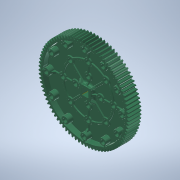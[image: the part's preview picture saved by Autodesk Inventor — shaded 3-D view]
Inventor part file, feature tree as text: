
AUTODESK INVENTOR PART (.ipt)
format: ipt  version: 2020 (Build 240168000, 168)  size: 7,812,608 bytes
history: native  units: in
note: dims shown in document units (in); Inventor stores cm internally (conversion verified against a paired STEP export)
features: other x3, plane x2, boolean_combine x1, imported_body x1
ambient origin geometry x8: Origin, YZ Plane, XZ Plane, XY Plane, X Axis, Y Axis, Z Axis, Center Point
bodies: Body1 (feature_tree)
feature tree (7):
  other  "Gear HS 84 tooth"
  boolean_combine  "Combine1"
  other  "Gear HS"
  other  "Work Axis1"
  imported_body  "Base1"
  plane  "Work Plane1"
  plane  "Work Plane2"
